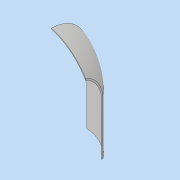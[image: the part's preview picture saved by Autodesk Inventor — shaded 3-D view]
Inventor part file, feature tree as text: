
AUTODESK INVENTOR PART (.ipt)
format: ipt  version: 2019 (Build 230136000, 136)  size: 284,160 bytes
history: native  units: mm
features: sketch x7, other x4, extrude x4, loft x1, shell x1, projected_geometry x1
ambient origin geometry x8: Origin, YZ Plane, XZ Plane, XY Plane, X Axis, Y Axis, Z Axis, Center Point
bodies: Body1 (feature_tree)
feature tree (18):
  other  "правое надкрылье"
  sketch  "Эскиз3"
  sketch  "Эскиз4"
  other  "РабПлоскость1"
  loft  "Лофт1"
  extrude  "Выдавливание2"  Depth=100.0mm
  shell  "Оболочка1"  Thickness=17.0mm
  extrude  "Выдавливание3"  Depth=4.0mm
  other  "РабПлоскость2"
  extrude  "Выдавливание7"  Depth=35.0mm
  other  "РабПлоскость3"
  extrude  "Выдавливание8"  TaperAngle=0.0deg  [1 undecoded]
  sketch  "Эскиз5"
  sketch  "Эскиз6"
  projected_geometry  "Спроецированная петля1"
  sketch  "Эскиз7"
  sketch  "Эскиз11"
  sketch  "Эскиз12"
note: 1 required parameter value undecoded (feature->parameter linkage not recoverable at this tier; creation-order binding heuristic only, values carry confidence <= 0.55)
